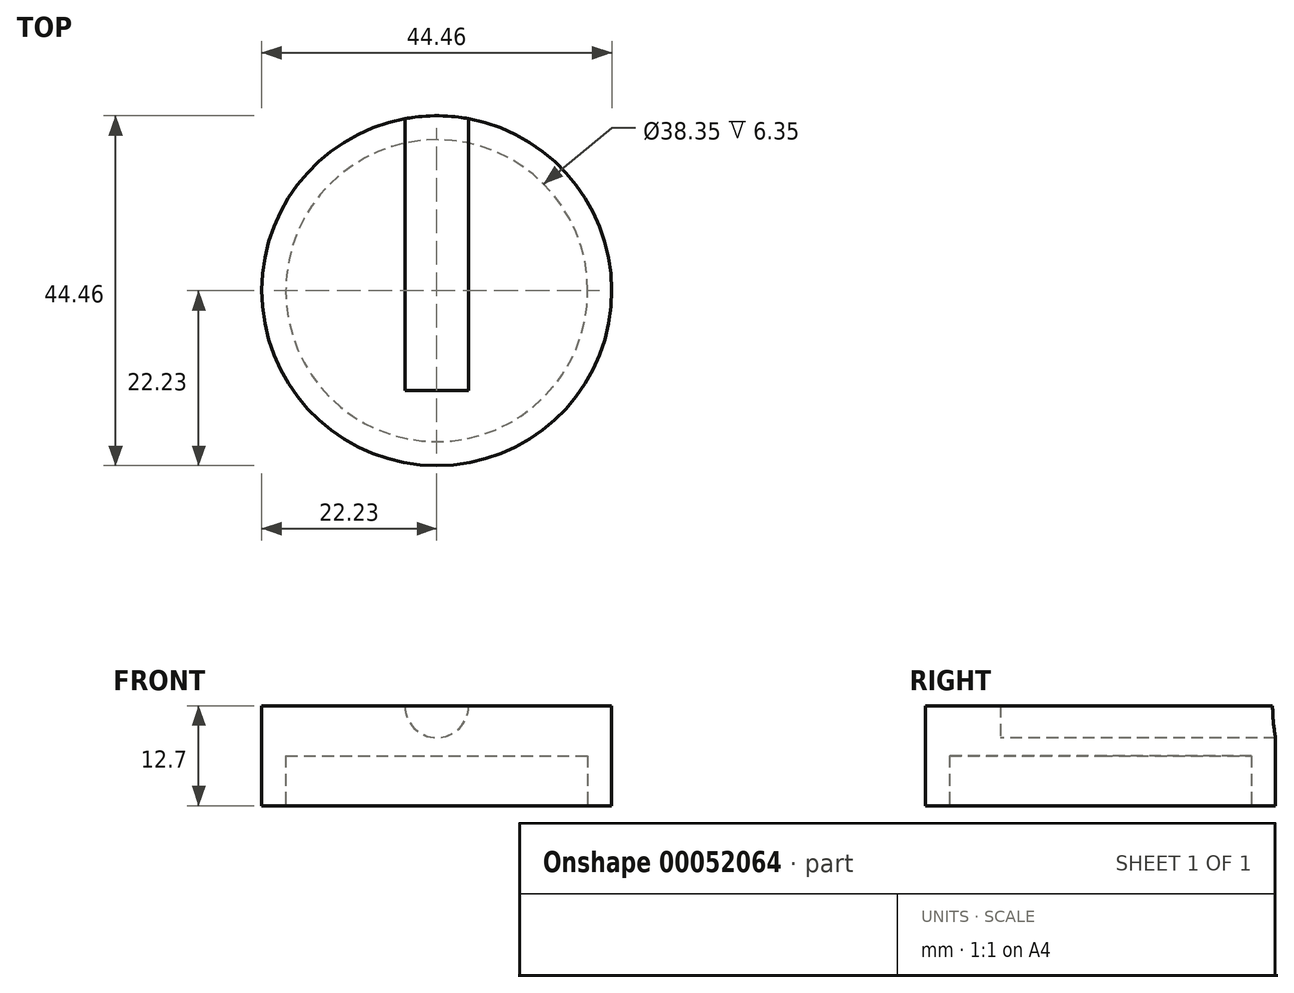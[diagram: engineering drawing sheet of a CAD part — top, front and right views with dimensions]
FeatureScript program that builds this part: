
annotation { "Feature Type Name" : "Feature", "Feature Type Description" : "" }
export const myFeature = defineFeature(function(context is Context, id is Id, definition is map)
    precondition{}
    {
        {
            var Q0;
            Q0=qCreatedBy(makeId("Top.planeOp"),FACE);
            var sketch = newSketch(context, id + "F0", { "sketchPlane" : qUnion([Q0])});
            skCircle(sketch, "E0", {"center": v(0, 0) * mm, "radius": 22.23 * mm});
            skSolve(sketch);
        }
        {
            var Q0;
            Q0=makeQuery(id+"F0.imprint","IMPRINT",FACE,{"disambiguationData":[TD([[makeQuery(id+"F0.imprint","IMPRINT",EDGE,{"derivedFrom":sQuery(id+"F0.wireOp",EDGE,"E0")}),1.0]])]});
            extrude(context, id + "F1", {"entities" : qUnion([Q0]), "depth" : 12.7 * mm});
        }
        {
            var Q0;
            Q0=makeQuery(id+"F1.opExtrude","CAP_FACE",FACE,{"disambiguationData":[OSD([sQuery(id+"F0.wireOp",EDGE,"E0")])],"isStart":true});
            var sketch = newSketch(context, id + "F2", { "sketchPlane" : qUnion([Q0])});
            skCircle(sketch, "E1", {"center": v(0, 0) * mm, "radius": 19.18 * mm});
            skSolve(sketch);
        }
        {
            var Q0;
            Q0 = qSketchRegion(id + "F2", true);
            extrude(context, id + "F3", {"entities" : qUnion([Q0]), "operationType" : NewBodyOperationType.REMOVE, "oppositeDirection" : true, "depth" : 6.35 * mm});
        }
        {
            var Q0;
            Q0=qCreatedBy(makeId("Front.planeOp"),FACE);
            var sketch = newSketch(context, id + "F4", { "sketchPlane" : qUnion([Q0])});
            skCircle(sketch, "E2", {"center": v(0, 12.7) * mm, "radius": 4.05 * mm});
            skSolve(sketch);
        }
        {
            var Q0;
            Q0 = qSketchRegion(id + "F4", true);
            extrude(context, id + "F5", {"entities" : qUnion([Q0]), "operationType" : NewBodyOperationType.REMOVE, "endBound" : BoundingType.THROUGH_ALL, "oppositeDirection" : true, "depth" : 25.4 * mm});
        }
        {
            var Q0;
            Q0 = qSketchRegion(id + "F4", true);
            extrude(context, id + "F6", {"entities" : qUnion([Q0]), "operationType" : NewBodyOperationType.REMOVE, "depth" : 12.7 * mm});
        }
    });
